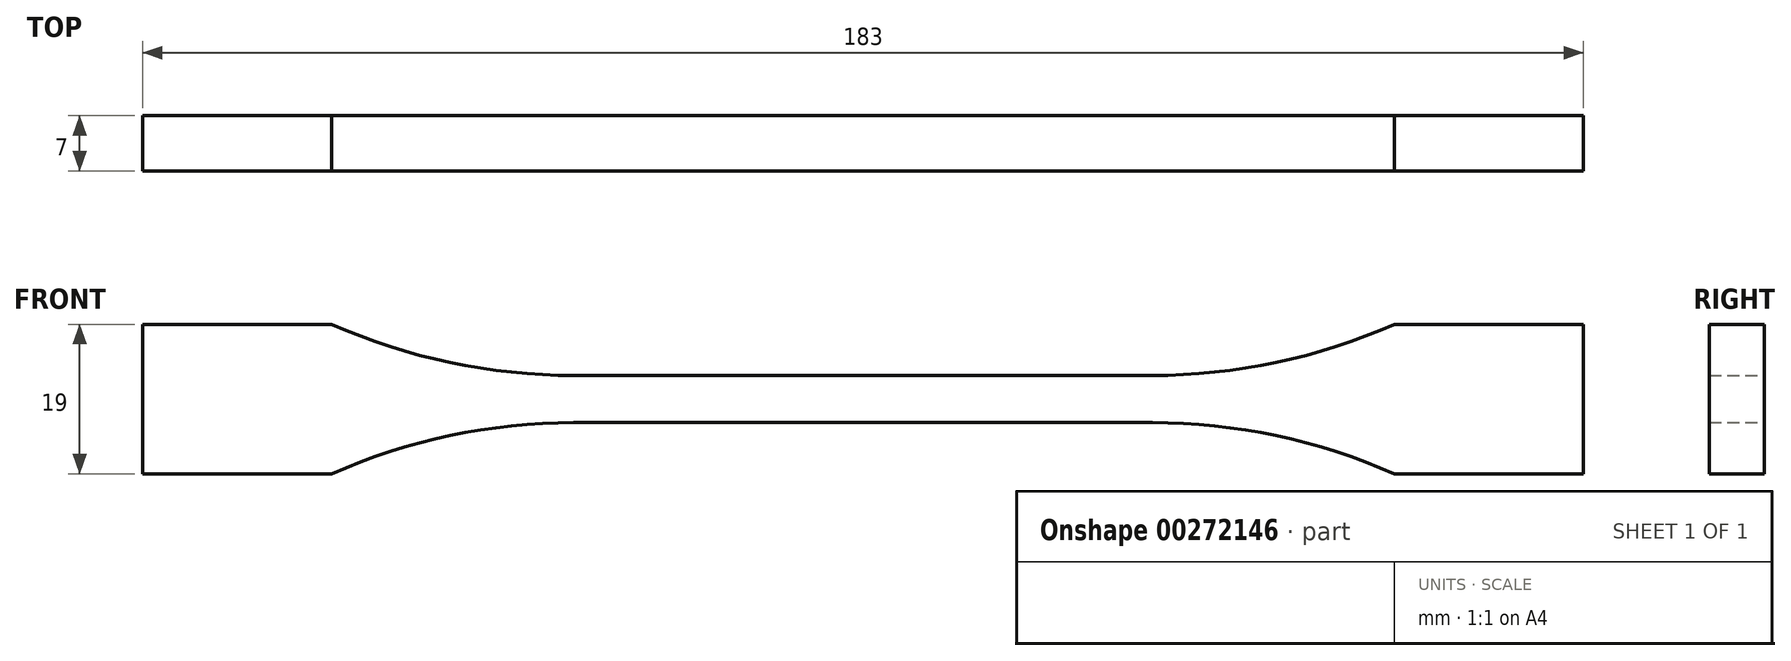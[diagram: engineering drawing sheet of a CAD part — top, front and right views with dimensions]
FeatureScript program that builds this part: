
annotation { "Feature Type Name" : "Feature", "Feature Type Description" : "" }
export const myFeature = defineFeature(function(context is Context, id is Id, definition is map)
    precondition{}
    {
        {
            var Q0;
            Q0=qCreatedBy(makeId("Front.planeOp"),FACE);
            var sketch = newSketch(context, id + "F0", { "sketchPlane" : qUnion([Q0])});
            skLineSegment(sketch, "E0", {"start": v(0, 3) * mm, "end": v(36.75, 3) * mm});
            skArc(sketch, "E1", {"start": v(36.75, 3) * mm, "mid": v(52.46, 4.64) * mm, "end": v(67.5, 9.5) * mm});
            skLineSegment(sketch, "E2", {"start": v(67.5, 9.5) * mm, "end": v(91.5, 9.5) * mm});
            skLineSegment(sketch, "E3", {"start": v(91.5, 9.5) * mm, "end": v(91.5, 0) * mm});
            skArc(sketch, "E4.MirrorCS", {"start": v(-36.75, 3) * mm, "mid": v(-52.46, 4.64) * mm, "end": v(-67.5, 9.5) * mm});
            skLineSegment(sketch, "E5.MirrorCS", {"start": v(-67.5, 9.5) * mm, "end": v(-91.5, 9.5) * mm});
            skLineSegment(sketch, "E6.MirrorCS", {"start": v(0, 3) * mm, "end": v(-36.75, 3) * mm});
            skLineSegment(sketch, "E7.MirrorCS", {"start": v(-91.5, 9.5) * mm, "end": v(-91.5, 0) * mm});
            skLineSegment(sketch, "E8.MirrorCS", {"start": v(67.5, -9.5) * mm, "end": v(91.5, -9.5) * mm});
            skArc(sketch, "E9.MirrorCS", {"start": v(36.75, -3) * mm, "mid": v(52.46, -4.64) * mm, "end": v(67.5, -9.5) * mm});
            skLineSegment(sketch, "E10.MirrorCS", {"start": v(-91.5, -9.5) * mm, "end": v(-91.5, 0) * mm});
            skLineSegment(sketch, "E11.MirrorCS", {"start": v(0, -3) * mm, "end": v(36.75, -3) * mm});
            skLineSegment(sketch, "E12.MirrorCS", {"start": v(-67.5, -9.5) * mm, "end": v(-91.5, -9.5) * mm});
            skLineSegment(sketch, "E13.MirrorCS", {"start": v(91.5, -9.5) * mm, "end": v(91.5, 0) * mm});
            skLineSegment(sketch, "E14.MirrorCS", {"start": v(0, -3) * mm, "end": v(-36.75, -3) * mm});
            skArc(sketch, "E15.MirrorCS", {"start": v(-36.75, -3) * mm, "mid": v(-52.46, -4.64) * mm, "end": v(-67.5, -9.5) * mm});
            skSolve(sketch);
        }
        {
            var Q0;
            Q0 = qSketchRegion(id + "F0", true);
            extrude(context, id + "F1", {"entities" : qUnion([Q0]), "depth" : 7 * mm});
        }
    });
